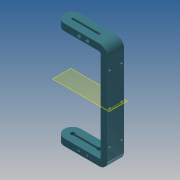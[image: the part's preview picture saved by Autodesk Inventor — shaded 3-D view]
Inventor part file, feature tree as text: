
AUTODESK INVENTOR PART (.ipt)
format: ipt  version: 2013 (Build 170138000, 138)  size: 260,096 bytes
history: native  units: mm
features: extrude x10, sketch x10, pattern_linear x2, projected_geometry x2, fillet x1, plane x1
ambient origin geometry x8: Origin, YZ Plane, XZ Plane, XY Plane, X Axis, Y Axis, Z Axis, Center Point
bodies: Solid1 (feature_tree)
feature tree (26):
  extrude  "Extrusion1"  Depth=25.0mm
  extrude  "Extrusion2"  Depth=160.0mm
  extrude  "Extrusion3"  Depth=10.0mm TaperAngle=0.0deg
  extrude  "Extrusion4"  Depth=5.0mm TaperAngle=0.0deg
  fillet  "Fillet2"  Radius=40.0mm
  extrude  "Extrusion11"  Depth=2.5mm
  extrude  "Extrusion12"  Depth=3.5mm
  extrude  "Extrusion13"  Depth=10.0mm TaperAngle=0.0deg
  extrude  "Extrusion14"  Depth=4.0mm TaperAngle=0.0deg
  pattern_linear  "Rectangular Pattern1"  Spacing1=12.5mm  [1 undecoded]
  extrude  "Extrusion15"  Depth=3.5mm
  extrude  "Extrusion16"  Depth=27.0mm
  plane  "Work Plane1"
  pattern_linear  "Rectangular Pattern2"  Spacing1=10.0mm  [1 undecoded]
  sketch  "Sketch1"  dims[d0=65.0mm d2=25.0mm]
  sketch  "Sketch2"  dims[d3=10.0mm d4=0.0mm d5=160.0mm]
  sketch  "Sketch3"  dims[d6=10.0mm d7=0.0mm d8=10.0mm d9=0.0mm]
  projected_geometry  "Projected Loop1"
  sketch  "Sketch4"  dims[d10=6.0mm d12=5.0mm d13=0.0mm d14=40.0mm]
  sketch  "Sketch11"  dims[d15=150.0mm d16=0.0mm d41=2.5mm d42=12.5mm]
  projected_geometry  "Projected Loop2"
  sketch  "Sketch12"  dims[d49=20.0mm d50=3.5mm]
  sketch  "Sketch13"  dims[d51=18.0mm d52=10.0mm d53=0.0mm]
  sketch  "Sketch14"  dims[d54=5.5mm d55=4.0mm d56=0.0mm]
  sketch  "Sketch15"  dims[d57=3.0mm]
  sketch  "Sketch16"  dims[d59=10.0mm d60=0.0mm d61=12.5mm d63=3.5mm d64=27.0mm d65=10.0mm d66=0.0mm d67=20.0mm d69=150.0mm d70=5.5mm d71=4.0mm d72=0.0mm d73=5.5mm d74=4.0mm d75=0.0mm d76=30.0mm d78=50.0mm]
note: 2 required parameter values undecoded (feature->parameter linkage not recoverable at this tier; creation-order binding heuristic only, values carry confidence <= 0.55)
